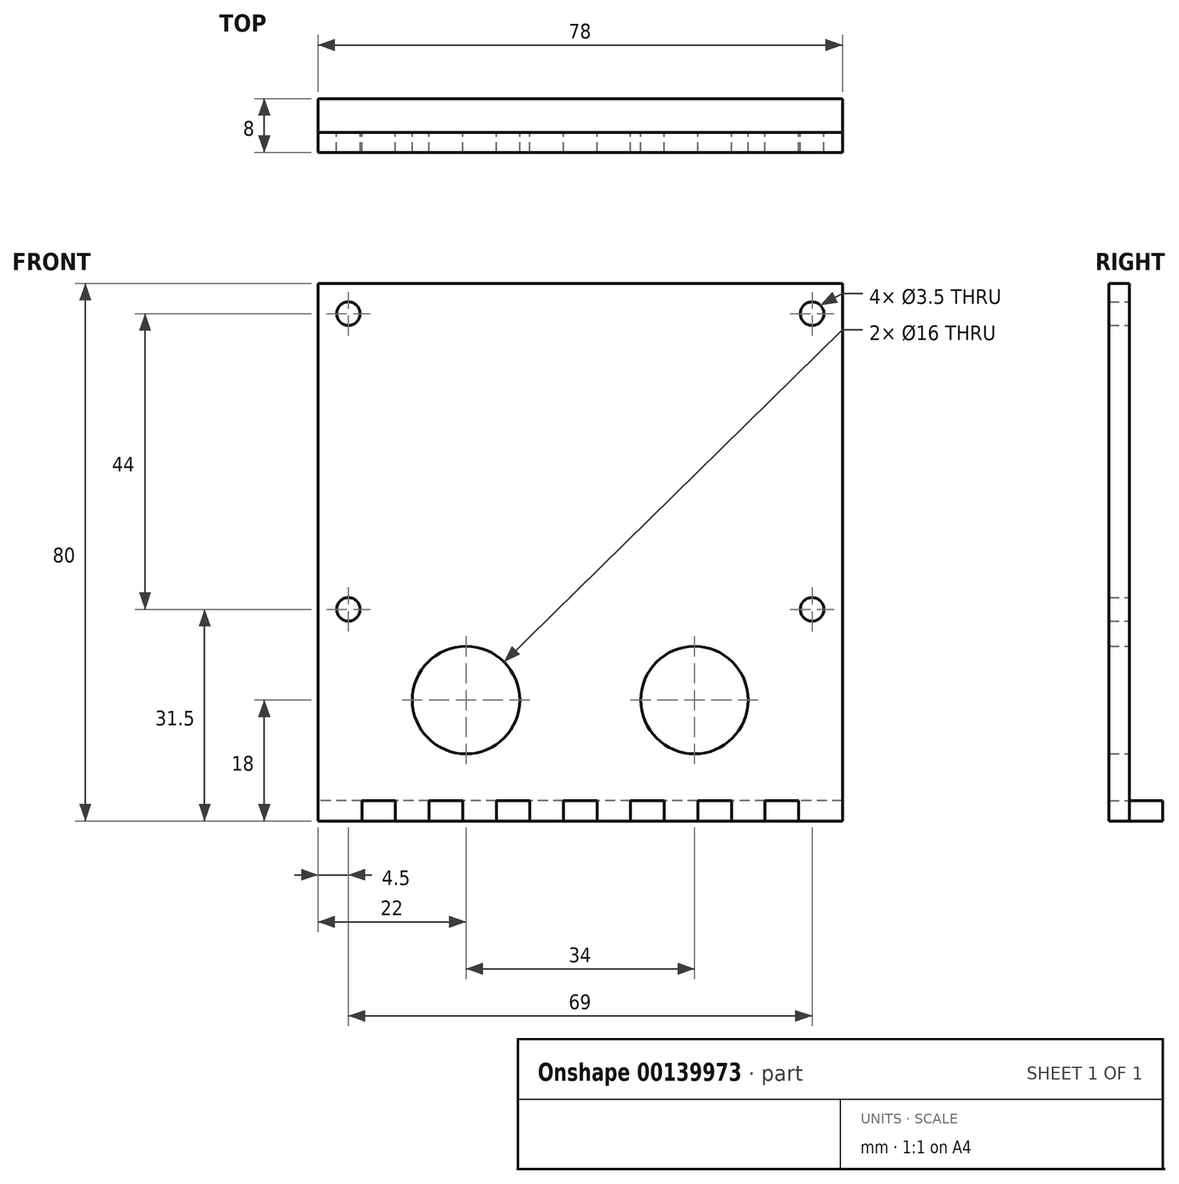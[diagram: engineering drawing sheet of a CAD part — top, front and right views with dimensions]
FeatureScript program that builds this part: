
annotation { "Feature Type Name" : "Feature", "Feature Type Description" : "" }
export const myFeature = defineFeature(function(context is Context, id is Id, definition is map)
    precondition{}
    {
        {
            var Q0;
            Q0=qCreatedBy(makeId("Front.planeOp"),FACE);
            var sketch = newSketch(context, id + "F0", { "sketchPlane" : qUnion([Q0])});
            skLineSegment(sketch, "E0.bottom", {"start": v(0, 0) * mm, "end": v(6.5, 0) * mm});
            skLineSegment(sketch, "E0.top", {"start": v(0, 80) * mm, "end": v(78, 80) * mm});
            skLineSegment(sketch, "E0.left", {"start": v(0, 0) * mm, "end": v(0, 80) * mm});
            skLineSegment(sketch, "E0.right", {"start": v(78, 0) * mm, "end": v(78, 80) * mm});
            skLineSegment(sketch, "E1", {"start": v(31.5, 3) * mm, "end": v(31.5, 0) * mm});
            skLineSegment(sketch, "E2", {"start": v(36.5, 0) * mm, "end": v(36.5, 3) * mm});
            skLineSegment(sketch, "E3", {"start": v(36.5, 3) * mm, "end": v(41.5, 3) * mm});
            skLineSegment(sketch, "E4", {"start": v(41.5, 3) * mm, "end": v(41.5, 0) * mm});
            skLineSegment(sketch, "E5", {"start": v(46.5, 0) * mm, "end": v(46.5, 3) * mm});
            skLineSegment(sketch, "E6", {"start": v(46.5, 3) * mm, "end": v(51.5, 3) * mm});
            skLineSegment(sketch, "E7", {"start": v(51.5, 3) * mm, "end": v(51.5, 0) * mm});
            skLineSegment(sketch, "E8", {"start": v(56.5, 0) * mm, "end": v(56.5, 3) * mm});
            skLineSegment(sketch, "E9", {"start": v(56.5, 3) * mm, "end": v(61.5, 3) * mm});
            skLineSegment(sketch, "E10", {"start": v(61.5, 3) * mm, "end": v(61.5, 0) * mm});
            skLineSegment(sketch, "E11", {"start": v(66.5, 0) * mm, "end": v(66.5, 3) * mm});
            skLineSegment(sketch, "E12", {"start": v(66.5, 3) * mm, "end": v(71.5, 3) * mm});
            skLineSegment(sketch, "E13", {"start": v(71.5, 3) * mm, "end": v(71.5, 0) * mm});
            skLineSegment(sketch, "E14.trimOffspring", {"start": v(31.5, 0) * mm, "end": v(36.5, 0) * mm});
            skLineSegment(sketch, "E15.trimOffspring", {"start": v(41.5, 0) * mm, "end": v(46.5, 0) * mm});
            skLineSegment(sketch, "E16.trimOffspring", {"start": v(51.5, 0) * mm, "end": v(56.5, 0) * mm});
            skLineSegment(sketch, "E17.trimOffspring", {"start": v(61.5, 0) * mm, "end": v(66.5, 0) * mm});
            skLineSegment(sketch, "E18.trimOffspring", {"start": v(71.5, 0) * mm, "end": v(78, 0) * mm});
            skLineSegment(sketch, "E19", {"start": v(6.5, 0) * mm, "end": v(6.5, 3) * mm});
            skLineSegment(sketch, "E20", {"start": v(6.5, 3) * mm, "end": v(11.5, 3) * mm});
            skLineSegment(sketch, "E21", {"start": v(11.5, 3) * mm, "end": v(11.5, 0) * mm});
            skLineSegment(sketch, "E22", {"start": v(11.5, 0) * mm, "end": v(16.5, 0) * mm});
            skLineSegment(sketch, "E23", {"start": v(16.5, 0) * mm, "end": v(16.5, 3) * mm});
            skLineSegment(sketch, "E24", {"start": v(16.5, 3) * mm, "end": v(21.5, 3) * mm});
            skLineSegment(sketch, "E25", {"start": v(21.5, 3) * mm, "end": v(21.5, 0) * mm});
            skLineSegment(sketch, "E26", {"start": v(21.5, 0) * mm, "end": v(26.5, 0) * mm});
            skLineSegment(sketch, "E27", {"start": v(26.5, 0) * mm, "end": v(26.5, 3) * mm});
            skLineSegment(sketch, "E28", {"start": v(26.5, 3) * mm, "end": v(31.5, 3) * mm});
            skLineSegment(sketch, "E29", {"start": v(78, 26) * mm, "end": v(38, 26) * mm});
            skLineSegment(sketch, "E30", {"start": v(38, 26) * mm, "end": v(38, 0) * mm});
            skLineSegment(sketch, "E31.bottom", {"start": v(4.5, 75.5) * mm, "end": v(73.5, 75.5) * mm, "construction": true});
            skLineSegment(sketch, "E31.top", {"start": v(4.5, 31.5) * mm, "end": v(73.5, 31.5) * mm, "construction": true});
            skLineSegment(sketch, "E31.left", {"start": v(4.5, 75.5) * mm, "end": v(4.5, 31.5) * mm, "construction": true});
            skLineSegment(sketch, "E31.right", {"start": v(73.5, 75.5) * mm, "end": v(73.5, 31.5) * mm, "construction": true});
            skLineSegment(sketch, "E32", {"start": v(0, 75.5) * mm, "end": v(4.5, 75.5) * mm, "construction": true});
            skLineSegment(sketch, "E33", {"start": v(4.5, 75.5) * mm, "end": v(4.5, 80) * mm, "construction": true});
            skLineSegment(sketch, "E34", {"start": v(73.5, 75.5) * mm, "end": v(78, 75.5) * mm, "construction": true});
            skCircle(sketch, "E35", {"center": v(4.5, 75.5) * mm, "radius": 1.75 * mm});
            skCircle(sketch, "E36", {"center": v(73.5, 75.5) * mm, "radius": 1.75 * mm});
            skCircle(sketch, "E37", {"center": v(4.5, 31.5) * mm, "radius": 1.75 * mm});
            skCircle(sketch, "E38", {"center": v(73.5, 31.5) * mm, "radius": 1.75 * mm});
            skCircle(sketch, "E39", {"center": v(22, 18) * mm, "radius": 8 * mm});
            skCircle(sketch, "E40", {"center": v(56, 18) * mm, "radius": 8 * mm});
            skLineSegment(sketch, "E41", {"start": v(39, 80) * mm, "end": v(39, 31.5) * mm, "construction": true});
            skSolve(sketch);
        }
        {
            var Q0;
            Q0=makeQuery(id+"F0.imprint","IMPRINT",FACE,{"disambiguationData":[TD([[makeQuery(id+"F0.imprint","IMPRINT",EDGE,{"derivedFrom":sQuery(id+"F0.wireOp",EDGE,"E0.bottom")}),1.0]])]});
            var Q1;
            {var subQ6=sQuery(id+"F0.wireOp",EDGE,"E4");Q1=makeQuery(id+"F0.imprint","IMPRINT",FACE,{"disambiguationData":[TD([[makeQuery(id+"F0.imprint","IMPRINT",EDGE,{"derivedFrom":subQ6}),1.0]])]});}
            extrude(context, id + "F1", {"entities" : qUnion([Q0, Q1]), "depth" : 3 * mm});
        }
        {
            var Q0;
            Q0=makeQuery(id+"F1.opExtrude","CAP_FACE",FACE,{"disambiguationData":[OSD([sQuery(id+"F0.wireOp",EDGE,"E0.bottom"),sQuery(id+"F0.wireOp",EDGE,"E0.top"),sQuery(id+"F0.wireOp",EDGE,"E0.left"),sQuery(id+"F0.wireOp",EDGE,"E0.right"),sQuery(id+"F0.wireOp",EDGE,"E1"),sQuery(id+"F0.wireOp",EDGE,"E2"),sQuery(id+"F0.wireOp",EDGE,"E3"),sQuery(id+"F0.wireOp",EDGE,"E4"),sQuery(id+"F0.wireOp",EDGE,"E5"),sQuery(id+"F0.wireOp",EDGE,"E6"),sQuery(id+"F0.wireOp",EDGE,"E7"),sQuery(id+"F0.wireOp",EDGE,"E8"),sQuery(id+"F0.wireOp",EDGE,"E9"),sQuery(id+"F0.wireOp",EDGE,"E10"),sQuery(id+"F0.wireOp",EDGE,"E11"),sQuery(id+"F0.wireOp",EDGE,"E12"),sQuery(id+"F0.wireOp",EDGE,"E13"),sQuery(id+"F0.wireOp",EDGE,"E14.trimOffspring"),sQuery(id+"F0.wireOp",EDGE,"E15.trimOffspring"),sQuery(id+"F0.wireOp",EDGE,"E16.trimOffspring"),sQuery(id+"F0.wireOp",EDGE,"E17.trimOffspring"),sQuery(id+"F0.wireOp",EDGE,"E18.trimOffspring"),sQuery(id+"F0.wireOp",EDGE,"E19"),sQuery(id+"F0.wireOp",EDGE,"E20"),sQuery(id+"F0.wireOp",EDGE,"E21"),sQuery(id+"F0.wireOp",EDGE,"E22"),sQuery(id+"F0.wireOp",EDGE,"E23"),sQuery(id+"F0.wireOp",EDGE,"E24"),sQuery(id+"F0.wireOp",EDGE,"E25"),sQuery(id+"F0.wireOp",EDGE,"E26"),sQuery(id+"F0.wireOp",EDGE,"E27"),sQuery(id+"F0.wireOp",EDGE,"E28")])],"isStart":false});
            var sketch = newSketch(context, id + "F2", { "sketchPlane" : qUnion([Q0])});
            skLineSegment(sketch, "E42.bottom", {"start": v(0, 0) * mm, "end": v(78, 0) * mm});
            skLineSegment(sketch, "E42.top", {"start": v(0, 3) * mm, "end": v(78, 3) * mm});
            skLineSegment(sketch, "E42.left", {"start": v(0, 0) * mm, "end": v(0, 3) * mm});
            skLineSegment(sketch, "E42.right", {"start": v(78, 0) * mm, "end": v(78, 3) * mm});
            skSolve(sketch);
        }
        {
            var Q0;
            {var subQ0=sQuery(id+"F2.wireOp",EDGE,"E42.left");Q0=makeQuery(id+"F2.imprint","IMPRINT",FACE,{"disambiguationData":[TD([[makeQuery(id+"F2.imprint","IMPRINT",EDGE,{"derivedFrom":subQ0}),-1.0]])]});}
            var Q1;
            {var subQ1=makeQuery(id+"F1.opExtrude","CAP_EDGE",EDGE,{"disambiguationData":[OSD([sQuery(id+"F0.wireOp",EDGE,"E19")])],"isStart":false});Q1=makeQuery(id+"F2.imprint","IMPRINT",FACE,{"disambiguationData":[TD([[makeQuery(id+"F2.imprint","IMPRINT",EDGE,{"derivedFrom":subQ1}),-1.0]])]});}
            var Q2;
            {var subQ1=makeQuery(id+"F1.opExtrude","CAP_EDGE",EDGE,{"disambiguationData":[OSD([sQuery(id+"F0.wireOp",EDGE,"E21")])],"isStart":false});Q2=makeQuery(id+"F2.imprint","IMPRINT",FACE,{"disambiguationData":[TD([[makeQuery(id+"F2.imprint","IMPRINT",EDGE,{"derivedFrom":subQ1}),1.0]])]});}
            var Q3;
            {var subQ1=makeQuery(id+"F1.opExtrude","CAP_EDGE",EDGE,{"disambiguationData":[OSD([sQuery(id+"F0.wireOp",EDGE,"E23")])],"isStart":false});Q3=makeQuery(id+"F2.imprint","IMPRINT",FACE,{"disambiguationData":[TD([[makeQuery(id+"F2.imprint","IMPRINT",EDGE,{"derivedFrom":subQ1}),-1.0]])]});}
            var Q4;
            {var subQ1=makeQuery(id+"F1.opExtrude","CAP_EDGE",EDGE,{"disambiguationData":[OSD([sQuery(id+"F0.wireOp",EDGE,"E25")])],"isStart":false});Q4=makeQuery(id+"F2.imprint","IMPRINT",FACE,{"disambiguationData":[TD([[makeQuery(id+"F2.imprint","IMPRINT",EDGE,{"derivedFrom":subQ1}),1.0]])]});}
            var Q5;
            {var subQ1=makeQuery(id+"F1.opExtrude","CAP_EDGE",EDGE,{"disambiguationData":[OSD([sQuery(id+"F0.wireOp",EDGE,"E1")])],"isStart":false});Q5=makeQuery(id+"F2.imprint","IMPRINT",FACE,{"disambiguationData":[TD([[makeQuery(id+"F2.imprint","IMPRINT",EDGE,{"derivedFrom":subQ1}),-1.0]])]});}
            var Q6;
            {var subQ1=makeQuery(id+"F1.opExtrude","CAP_EDGE",EDGE,{"disambiguationData":[OSD([sQuery(id+"F0.wireOp",EDGE,"E1")])],"isStart":false});Q6=makeQuery(id+"F2.imprint","IMPRINT",FACE,{"disambiguationData":[TD([[makeQuery(id+"F2.imprint","IMPRINT",EDGE,{"derivedFrom":subQ1}),1.0]])]});}
            var Q7;
            {var subQ1=makeQuery(id+"F1.opExtrude","CAP_EDGE",EDGE,{"disambiguationData":[OSD([sQuery(id+"F0.wireOp",EDGE,"E2")])],"isStart":false});Q7=makeQuery(id+"F2.imprint","IMPRINT",FACE,{"disambiguationData":[TD([[makeQuery(id+"F2.imprint","IMPRINT",EDGE,{"derivedFrom":subQ1}),-1.0]])]});}
            var Q8;
            {var subQ1=makeQuery(id+"F1.opExtrude","CAP_EDGE",EDGE,{"disambiguationData":[OSD([sQuery(id+"F0.wireOp",EDGE,"E4")])],"isStart":false});Q8=makeQuery(id+"F2.imprint","IMPRINT",FACE,{"disambiguationData":[TD([[makeQuery(id+"F2.imprint","IMPRINT",EDGE,{"derivedFrom":subQ1}),1.0]])]});}
            var Q9;
            {var subQ1=makeQuery(id+"F1.opExtrude","CAP_EDGE",EDGE,{"disambiguationData":[OSD([sQuery(id+"F0.wireOp",EDGE,"E5")])],"isStart":false});Q9=makeQuery(id+"F2.imprint","IMPRINT",FACE,{"disambiguationData":[TD([[makeQuery(id+"F2.imprint","IMPRINT",EDGE,{"derivedFrom":subQ1}),-1.0]])]});}
            var Q10;
            {var subQ1=makeQuery(id+"F1.opExtrude","CAP_EDGE",EDGE,{"disambiguationData":[OSD([sQuery(id+"F0.wireOp",EDGE,"E7")])],"isStart":false});Q10=makeQuery(id+"F2.imprint","IMPRINT",FACE,{"disambiguationData":[TD([[makeQuery(id+"F2.imprint","IMPRINT",EDGE,{"derivedFrom":subQ1}),1.0]])]});}
            var Q11;
            {var subQ1=makeQuery(id+"F1.opExtrude","CAP_EDGE",EDGE,{"disambiguationData":[OSD([sQuery(id+"F0.wireOp",EDGE,"E8")])],"isStart":false});Q11=makeQuery(id+"F2.imprint","IMPRINT",FACE,{"disambiguationData":[TD([[makeQuery(id+"F2.imprint","IMPRINT",EDGE,{"derivedFrom":subQ1}),-1.0]])]});}
            var Q12;
            {var subQ1=makeQuery(id+"F1.opExtrude","CAP_EDGE",EDGE,{"disambiguationData":[OSD([sQuery(id+"F0.wireOp",EDGE,"E10")])],"isStart":false});Q12=makeQuery(id+"F2.imprint","IMPRINT",FACE,{"disambiguationData":[TD([[makeQuery(id+"F2.imprint","IMPRINT",EDGE,{"derivedFrom":subQ1}),1.0]])]});}
            var Q13;
            {var subQ1=makeQuery(id+"F1.opExtrude","CAP_EDGE",EDGE,{"disambiguationData":[OSD([sQuery(id+"F0.wireOp",EDGE,"E11")])],"isStart":false});Q13=makeQuery(id+"F2.imprint","IMPRINT",FACE,{"disambiguationData":[TD([[makeQuery(id+"F2.imprint","IMPRINT",EDGE,{"derivedFrom":subQ1}),-1.0]])]});}
            var Q14;
            {var subQ0=sQuery(id+"F2.wireOp",EDGE,"E42.right");Q14=makeQuery(id+"F2.imprint","IMPRINT",FACE,{"disambiguationData":[TD([[makeQuery(id+"F2.imprint","IMPRINT",EDGE,{"derivedFrom":subQ0}),1.0]])]});}
            extrude(context, id + "F3", {"entities" : qUnion([Q0, Q1, Q2, Q3, Q4, Q5, Q6, Q7, Q8, Q9, Q10, Q11, Q12, Q13, Q14]), "oppositeDirection" : true, "depth" : 8 * mm});
        }
        {
            var Q0;
            Q0=makeQuery(id+"F1.opExtrude","SWEPT_BODY",BODY,{"disambiguationData":[OSD([sQuery(id+"F0.wireOp",EDGE,"E0.bottom"),sQuery(id+"F0.wireOp",EDGE,"E0.top"),sQuery(id+"F0.wireOp",EDGE,"E0.left"),sQuery(id+"F0.wireOp",EDGE,"E0.right"),sQuery(id+"F0.wireOp",EDGE,"E1"),sQuery(id+"F0.wireOp",EDGE,"E2"),sQuery(id+"F0.wireOp",EDGE,"E3"),sQuery(id+"F0.wireOp",EDGE,"E4"),sQuery(id+"F0.wireOp",EDGE,"E5"),sQuery(id+"F0.wireOp",EDGE,"E6"),sQuery(id+"F0.wireOp",EDGE,"E7"),sQuery(id+"F0.wireOp",EDGE,"E8"),sQuery(id+"F0.wireOp",EDGE,"E9"),sQuery(id+"F0.wireOp",EDGE,"E10"),sQuery(id+"F0.wireOp",EDGE,"E11"),sQuery(id+"F0.wireOp",EDGE,"E12"),sQuery(id+"F0.wireOp",EDGE,"E13"),sQuery(id+"F0.wireOp",EDGE,"E14.trimOffspring"),sQuery(id+"F0.wireOp",EDGE,"E15.trimOffspring"),sQuery(id+"F0.wireOp",EDGE,"E16.trimOffspring"),sQuery(id+"F0.wireOp",EDGE,"E17.trimOffspring"),sQuery(id+"F0.wireOp",EDGE,"E18.trimOffspring"),sQuery(id+"F0.wireOp",EDGE,"E19"),sQuery(id+"F0.wireOp",EDGE,"E20"),sQuery(id+"F0.wireOp",EDGE,"E21"),sQuery(id+"F0.wireOp",EDGE,"E22"),sQuery(id+"F0.wireOp",EDGE,"E23"),sQuery(id+"F0.wireOp",EDGE,"E24"),sQuery(id+"F0.wireOp",EDGE,"E25"),sQuery(id+"F0.wireOp",EDGE,"E26"),sQuery(id+"F0.wireOp",EDGE,"E27"),sQuery(id+"F0.wireOp",EDGE,"E28")])]});
            var Q1;
            Q1=makeQuery(id+"F3.opExtrude","SWEPT_BODY",BODY,{"disambiguationData":[OSD([sQuery(id+"F2.wireOp",EDGE,"E42.bottom"),sQuery(id+"F2.wireOp",EDGE,"E42.top"),sQuery(id+"F2.wireOp",EDGE,"E42.left"),sQuery(id+"F2.wireOp",EDGE,"E42.right")])]});
            booleanBodies(context, id + "F4", {"operationType" : BooleanOperationType.SUBTRACTION, "tools" : qUnion([Q0]), "targets" : qUnion([Q1]), "keepTools" : true});
        }
    });
